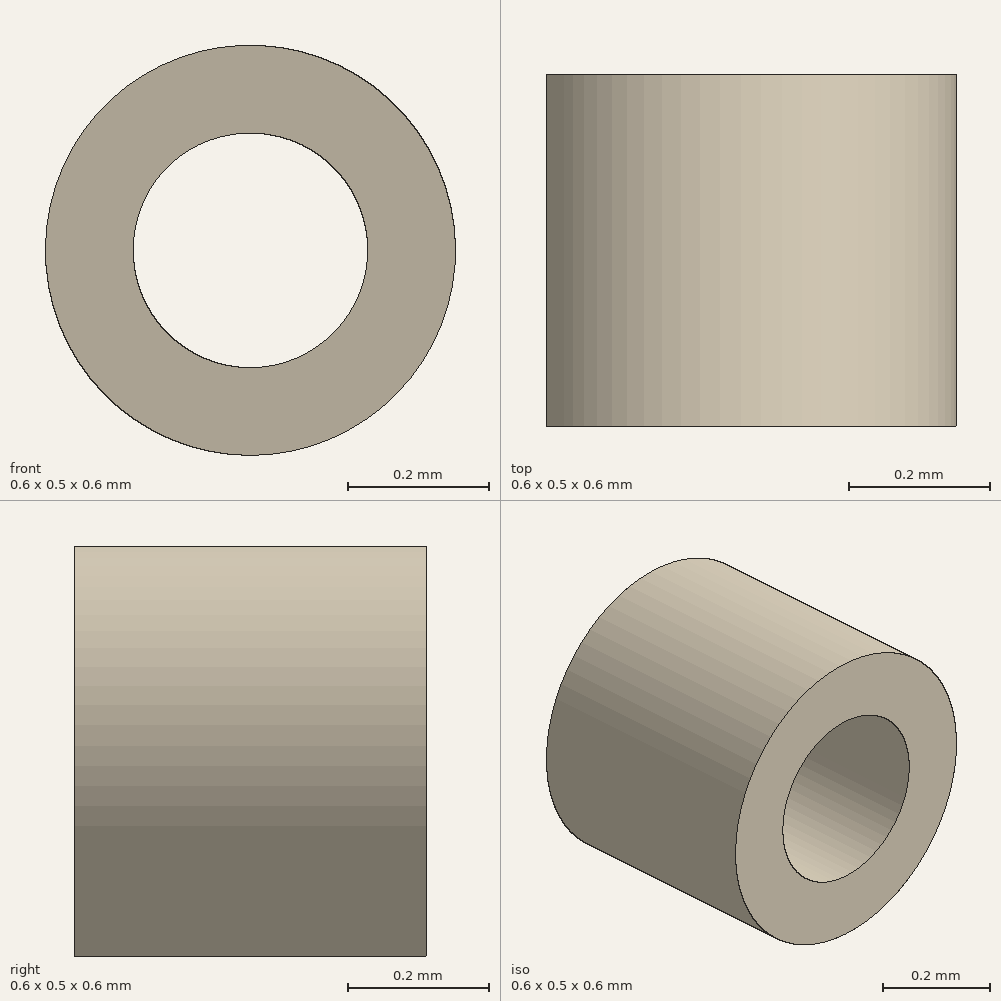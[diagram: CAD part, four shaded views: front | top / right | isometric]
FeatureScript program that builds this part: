
annotation { "Feature Type Name" : "Feature", "Feature Type Description" : "" }
export const myFeature = defineFeature(function(context is Context, id is Id, definition is map)
    precondition{}
    {
        {
            var Q0;
            Q0=qCreatedBy(makeId("Front.planeOp"),FACE);
            var sketch = newSketch(context, id + "F0", { "sketchPlane" : qUnion([Q0])});
            skCircle(sketch, "E0", {"center": v(0, 0) * mm, "radius": 0.3 * mm});
            skCircle(sketch, "E1", {"center": v(0, 0) * mm, "radius": 0.17 * mm});
            skSolve(sketch);
        }
        {
            var Q0;
            Q0=makeQuery(id+"F0.imprint","IMPRINT",FACE,{"disambiguationData":[TD([[makeQuery(id+"F0.imprint","IMPRINT",EDGE,{"derivedFrom":sQuery(id+"F0.wireOp",EDGE,"E0")}),1.0]])]});
            extrude(context, id + "F1", {"entities" : qUnion([Q0]), "depth" : 0.5 * mm});
        }
    });
